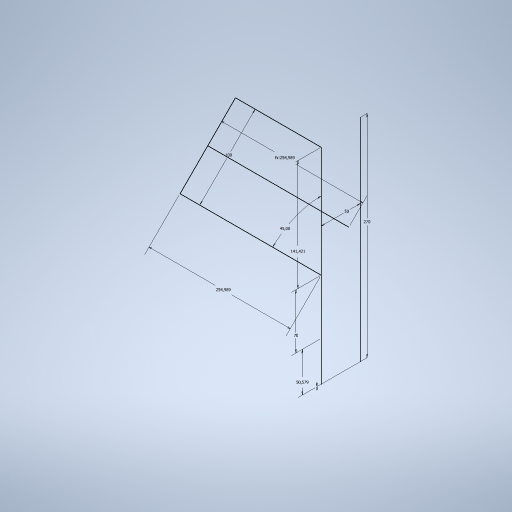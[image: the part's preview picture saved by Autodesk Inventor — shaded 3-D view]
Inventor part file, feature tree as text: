
AUTODESK INVENTOR PART (.ipt)
format: ipt  version: 2024.3 (Build 283343000, 343)  size: 243,200 bytes
history: native  units: mm
features: sketch x1
ambient origin geometry x8: Origin, YZ Plane, XZ Plane, XY Plane, X Axis, Y Axis, Z Axis, Center Point
feature tree (1):
  sketch  "Sketch1"  dims[d0=270.0mm d1=50.579mm d2=70.0mm d3=141.421mm d4=45.0deg d5=100.0mm d6=50.0mm d7=254.989146mm d8=254.989146mm d9=0.0mm]
